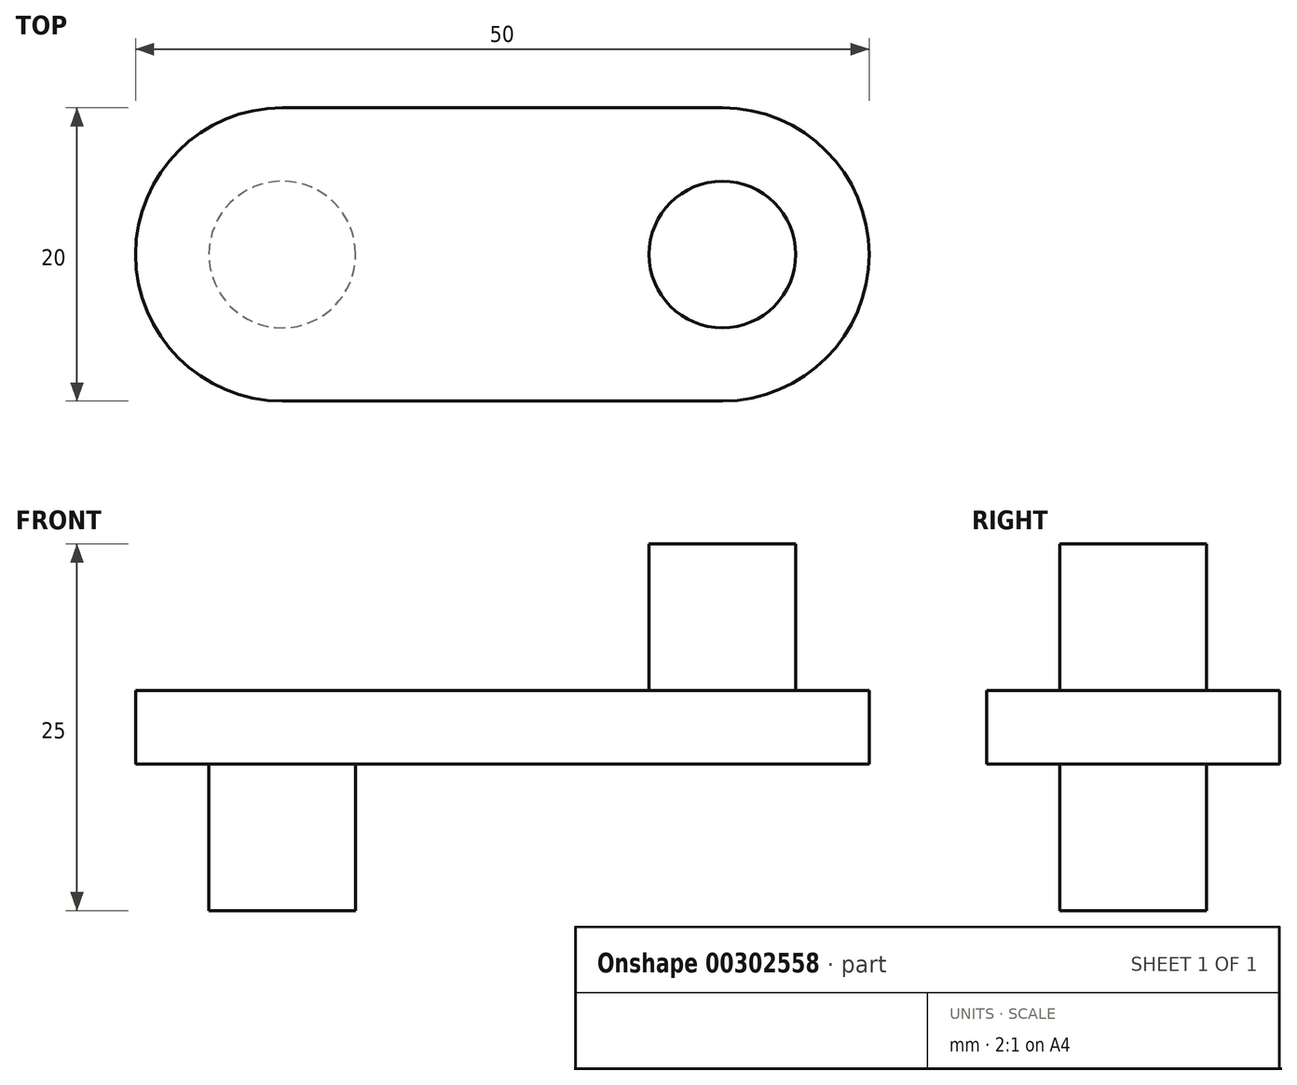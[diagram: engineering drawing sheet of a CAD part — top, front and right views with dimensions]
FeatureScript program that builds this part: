
annotation { "Feature Type Name" : "Feature", "Feature Type Description" : "" }
export const myFeature = defineFeature(function(context is Context, id is Id, definition is map)
    precondition{}
    {
        {
            var Q0;
            Q0=qCreatedBy(makeId("Top.planeOp"),FACE);
            var sketch = newSketch(context, id + "F0", { "sketchPlane" : qUnion([Q0])});
            skLineSegment(sketch, "E0", {"start": v(-15, 0) * mm, "end": v(15, 0) * mm, "construction": true});
            skCircle(sketch, "E1", {"center": v(-15, 0) * mm, "radius": 5 * mm, "construction": true});
            skCircle(sketch, "E2", {"center": v(15, 0) * mm, "radius": 5 * mm, "construction": true});
            skLineSegment(sketch, "E3", {"start": v(-15, 10) * mm, "end": v(15, 10) * mm});
            skLineSegment(sketch, "E4", {"start": v(-15, -10) * mm, "end": v(15, -10) * mm});
            skArc(sketch, "E5", {"start": v(-15, 10) * mm, "mid": v(-25, 0) * mm, "end": v(-15, -10) * mm});
            skArc(sketch, "E6", {"start": v(15, -10) * mm, "mid": v(25, 0) * mm, "end": v(15, 10) * mm});
            skSolve(sketch);
        }
        {
            var Q0;
            Q0 = qSketchRegion(id + "F0", true);
            extrude(context, id + "F1", {"entities" : qUnion([Q0]), "depth" : 5 * mm});
        }
        {
            var Q0;
            Q0=makeQuery(id+"F1.opExtrude","CAP_FACE",FACE,{"disambiguationData":[OSD([sQuery(id+"F0.wireOp",EDGE,"E3"),sQuery(id+"F0.wireOp",EDGE,"E4"),sQuery(id+"F0.wireOp",EDGE,"E5"),sQuery(id+"F0.wireOp",EDGE,"E6")])],"isStart":false});
            var sketch = newSketch(context, id + "F2", { "sketchPlane" : qUnion([Q0])});
            skLineSegment(sketch, "E7", {"start": v(-15, 0) * mm, "end": v(15, 0) * mm, "construction": true});
            skCircle(sketch, "E8", {"center": v(-15, 0) * mm, "radius": 5 * mm});
            skCircle(sketch, "E9", {"center": v(15, 0) * mm, "radius": 5 * mm});
            skSolve(sketch);
        }
        {
            var Q0;
            Q0=makeQuery(id+"F2.imprint","IMPRINT",FACE,{"disambiguationData":[TD([[makeQuery(id+"F2.imprint","IMPRINT",EDGE,{"derivedFrom":sQuery(id+"F2.wireOp",EDGE,"E8")}),1.0]])]});
            var Q1;
            Q1 = qConstructionFilter(qBodyType(qCreatedBy(id + "F2" ,EDGE), BodyType.WIRE), ConstructionObject.NO);
            extrude(context, id + "F3", {"entities" : qUnion([Q0]), "operationType" : NewBodyOperationType.ADD, "surfaceEntities" : qUnion([Q1]), "oppositeDirection" : true, "depth" : 15 * mm});
        }
        {
            var Q0;
            Q0=makeQuery(id+"F1.opExtrude","CAP_FACE",FACE,{"disambiguationData":[OSD([sQuery(id+"F0.wireOp",EDGE,"E3"),sQuery(id+"F0.wireOp",EDGE,"E4"),sQuery(id+"F0.wireOp",EDGE,"E5"),sQuery(id+"F0.wireOp",EDGE,"E6")])],"isStart":false});
            var sketch = newSketch(context, id + "F4", { "sketchPlane" : qUnion([Q0])});
            skCircle(sketch, "E10", {"center": v(15, 0) * mm, "radius": 5 * mm});
            skSolve(sketch);
        }
        {
            var Q0;
            Q0 = qSketchRegion(id + "F4", true);
            extrude(context, id + "F5", {"entities" : qUnion([Q0]), "operationType" : NewBodyOperationType.ADD, "depth" : 10 * mm});
        }
    });
